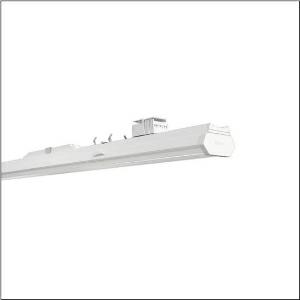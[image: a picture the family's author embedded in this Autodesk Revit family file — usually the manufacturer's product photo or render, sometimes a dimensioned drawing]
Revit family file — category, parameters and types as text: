
# Revit family: licross_11_protected_mo_51td1bcn485g
name_source: partatom
category: Lighting Fixtures
units: mm (PartAtom-declared; Revit-internal decimal feet)

## family parameters
Cut with Voids When Loaded = No
Host = Face
Light Source = No
Part Type = Normal
Room Calculation Point = No
Round Connector Dimension = Use Diameter
Shared = No

## types (1)
- --- (1 x LED, 8520 lm, 49.4 W, 4000K)
    Apparent Load = 49 VA
    CIE Flux Codes = 54 82 95 97 100
    Color Rendering = 80
    Color Temperature = 4000K
    Default Elevation = 1800 mm
    Description = Licross 11 Protected MO, luminaire insert, of sheet steel, galvanised, coil coated, white, length: 1.500mm, width: 90mm, height: 101mm, LED rated luminous flux: 8.520lm, light colour: 840, SDCM (Standard Deviation of Colour Matching)MacAdam ≤ 2 SDCM (initial), control gear: ON/OFF Multilumen, CLOi, with plug, 3-pole, with phase selection, mains connection: 220..240V, AC, 50/60Hz, start of lifetime: 49W, end of service life: 55W, internal wiring halogen-free, primary optical cover: cover, of PMMA, light emission: direct distribution, primary light characteristic: symmetric, protection rating (complete): IP54, insulation class (complete): insulation class I (protective earthing), certification: CE, ENEC, VDE, UKCA, protection symbol: D if used in an environment with non-conductive dust loads with corresponding accessories, impact resistance: IK06, permissible ambient temperature for indoor applications: -35..+40°C, corresponds to IFS (International Featured Standards) requirements for safety and quality in the food industry, reducing of maximum allowable ambient temperature of 5°C with ceiling mounting, LABS conformity tested according to VDMA 24364:2018-05, The light source and the operating device comply with the requirements of the Ecodesign Regulation (EU) 2019/2020 and are replaceable in accordance with this regulation, packaging unit: 1 piece
    Height = 92 mm
    Lamp = 1 x LED
    Lamp Light Flux = 8520 lm
    Lamp Power = 49.4 W
    Lamp count = 1
    Length = 1500 mm
    Luminous efficacy = 172 lm/W
    Manufacturer = Siteco
    ModVariant = No
    Model = 51TD1BCN485G
    Mounting Place = Ceiling
    Mounting Type = Pendant
    Number of Poles = 1
    OnlyDefault = Yes
    Power Factor = 1
    Product Name = Licross 11 Protected MO
    Product group = luminaire insert | ceiling pendant
    ProductGroupID = 901
    Protection Class = Protection class I
    Protection Degree = IP 54
    RLX_Detail_Level = 1
    RLX_Emergency_Light_Flux = 0 lm
    RLX_Emergency_Type = 0
    RLX_Emergency_Type_DB = No
    RlxData = <blob elided: 22301 chars, md5=23809b6e>
    Socket = socket
    Standby Power = 0 W
    System Light Flux = 8520 lm
    System Power = 49 W
    Type Comments = factory setting: luminous flux: 100 % | (A | C | E) | 113 mA
    Type Image = l_1256145.jpg
    URL = http://relux.com
    VarID = @adj_091349
    Voltage = 0 V
    Weight = 0.00 kg
    Width = 88 mm

## geometry (parser evidence)
native form markers: Blend x4, Sweep x11
no freeform markers — native parametric forms only
